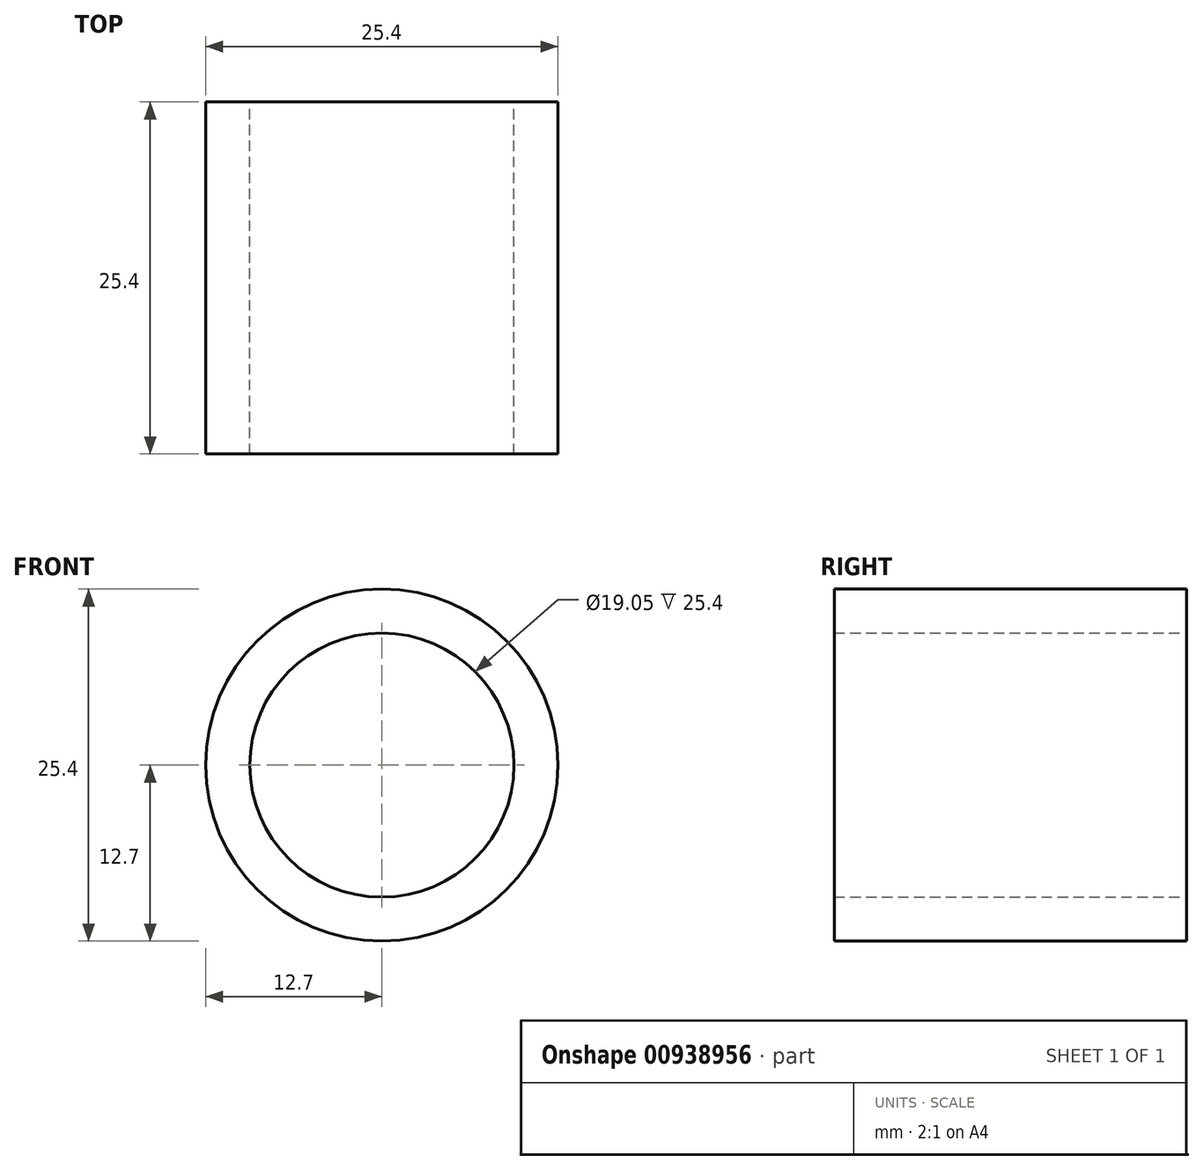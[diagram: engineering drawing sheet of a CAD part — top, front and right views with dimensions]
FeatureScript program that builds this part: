
annotation { "Feature Type Name" : "Feature", "Feature Type Description" : "" }
export const myFeature = defineFeature(function(context is Context, id is Id, definition is map)
    precondition{}
    {
        {
            var Q0;
            Q0=qCreatedBy(makeId("Front.planeOp"),FACE);
            var sketch = newSketch(context, id + "F0", { "sketchPlane" : qUnion([Q0])});
            skCircle(sketch, "E0", {"center": v(0, 0) * mm, "radius": 12.7 * mm});
            skCircle(sketch, "E1", {"center": v(0, 0) * mm, "radius": 9.53 * mm});
            skSolve(sketch);
        }
        {
            var Q0;
            Q0 = qSketchRegion(id + "F0", true);
            extrude(context, id + "F1", {"entities" : qUnion([Q0]), "depth" : 25.4 * mm, "offsetDistance" : 25.4 * mm});
        }
    });
